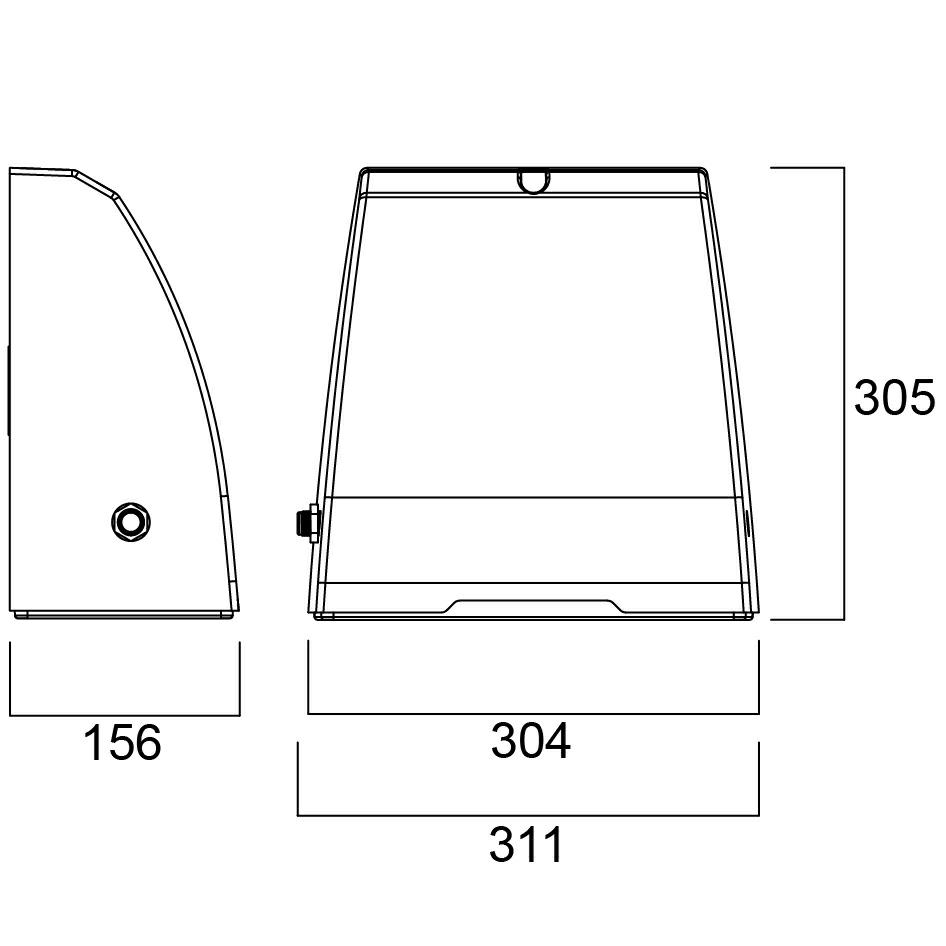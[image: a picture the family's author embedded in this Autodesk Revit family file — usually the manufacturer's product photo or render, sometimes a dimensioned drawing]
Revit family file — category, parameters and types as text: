
# Revit family: 0049945_3250lm
name_source: partatom
category: Lighting Fixtures
revit_build: Autodesk Revit 2018 (Build: 20170223_1515(x64)
units: mm (PartAtom-declared; Revit-internal decimal feet)

## family parameters
Cut with Voids When Loaded = No
Host = Face
Light Source = Yes
OmniClass Number = 23.80.70.00
OmniClass Title = Lighting
Part Type = Normal
Room Calculation Point = No
Round Connector Dimension = Use Diameter
Shared = No

## types (1)
- 0049945 MURO SURF IP65 1700-3250LM 840 PH E3 GR
    Apparent Load = 30 VA
    Assembly Code = D5020200
    AssetType = Fixed
    ClassificationName = Uniclass2015
    ClassificationValue = EF_70_80
    Color Filter = 16777215
    Cost = 0 $
    Default Elevation = 1219 mm
    Description = Muro Surface is a wall mounted fixture for exterior lighting applications with 3 hours combined non-maintained emergency unit. Comes with aluminium housing in RAL7016 anthracite grey colour, frosted PC diffuser, IP65, IK10, Class I, 4000K, non-dimmable multipower driver with 5 settings, 1700 / 1900 / 2750 / 3150 / 3250 lm, 16 / 18 / 26 / 29 / 30 W, up to 109 lm/W total system efficacy, switchable built in Mini photocell, CRI80, Asymmetrical beam, 119.000 hrs L70B50 lifespan, 304 x 305 x 155 mm (L x W x D) dimensions, 4.32 kg weight.
    Dimming Lamp Color Temperature Shift = <None>
    DocumentationLiterature = http://www.sylvania-lighting.com
    ElectricShockClassification = 108
    Emit Shape Visible in Rendering = No
    Emit from Circle Diameter = 610 mm
    IfcExportAs = Class I
    IfcExportType = IfcLightFixtureType
    ImpactProtectionIndex = IfcLightFixtureType
    IngressProtection = IfcLightFixtureType
    InputNominalFrequency = 4000
    InputVoltage = 0
    LampColourRenderingIndex = 16500
    LampColourTemperature = LED
    LampMacAdamStep = 80
    LampNominalLuminous = 4000 K
    LightOutputRatio = LED
    LuminaireType = 0
    ManufacturerName = 108 lm/W
    Material = Feilo Sylvania
    Material_1_SYL = <By Category>
    Material_2_SYL = <By Category>
    Material_3_SYL = <By Category>
    Material_4_SYL = <By Category>
    Model = Muro Surface IP65 1700-3250lm 840 PH E3 Grey
    ModelNumber = 0049945
    ModelReference = Muro Surface IP65 1700-3250lm 840 PH E3 Grey
    Name = Muro Surface IP65 1700-3250lm 840 PH E3 Grey
    NominalDepth = 155 mm  [stored 0.50853 ft]
    NominalHeight = 305 mm  [stored 1.00066 ft]
    NominalLength = 155 mm  [stored 0.50853 ft]
    Photometric Web File = 0049945_3250lm.IES
    PowerConsumption = Lighting
    PowerFactor = 0.95
    Tilt Angle = -90.00°
    Type Image = <None>
    TypeName = Muro Surface IP65 1700-3250lm 840 PH E3 Grey
    URL = 0.9
    Voltage = 0 V
    WarrantyDescription = http://www.sylvania-lighting.com

note: [stored X ft] marks values corroborated as IEEE doubles in the binary element streams (Revit-internal decimal feet)

## geometry (parser evidence)
native form markers: Sweep x1
no freeform markers — native parametric forms only
